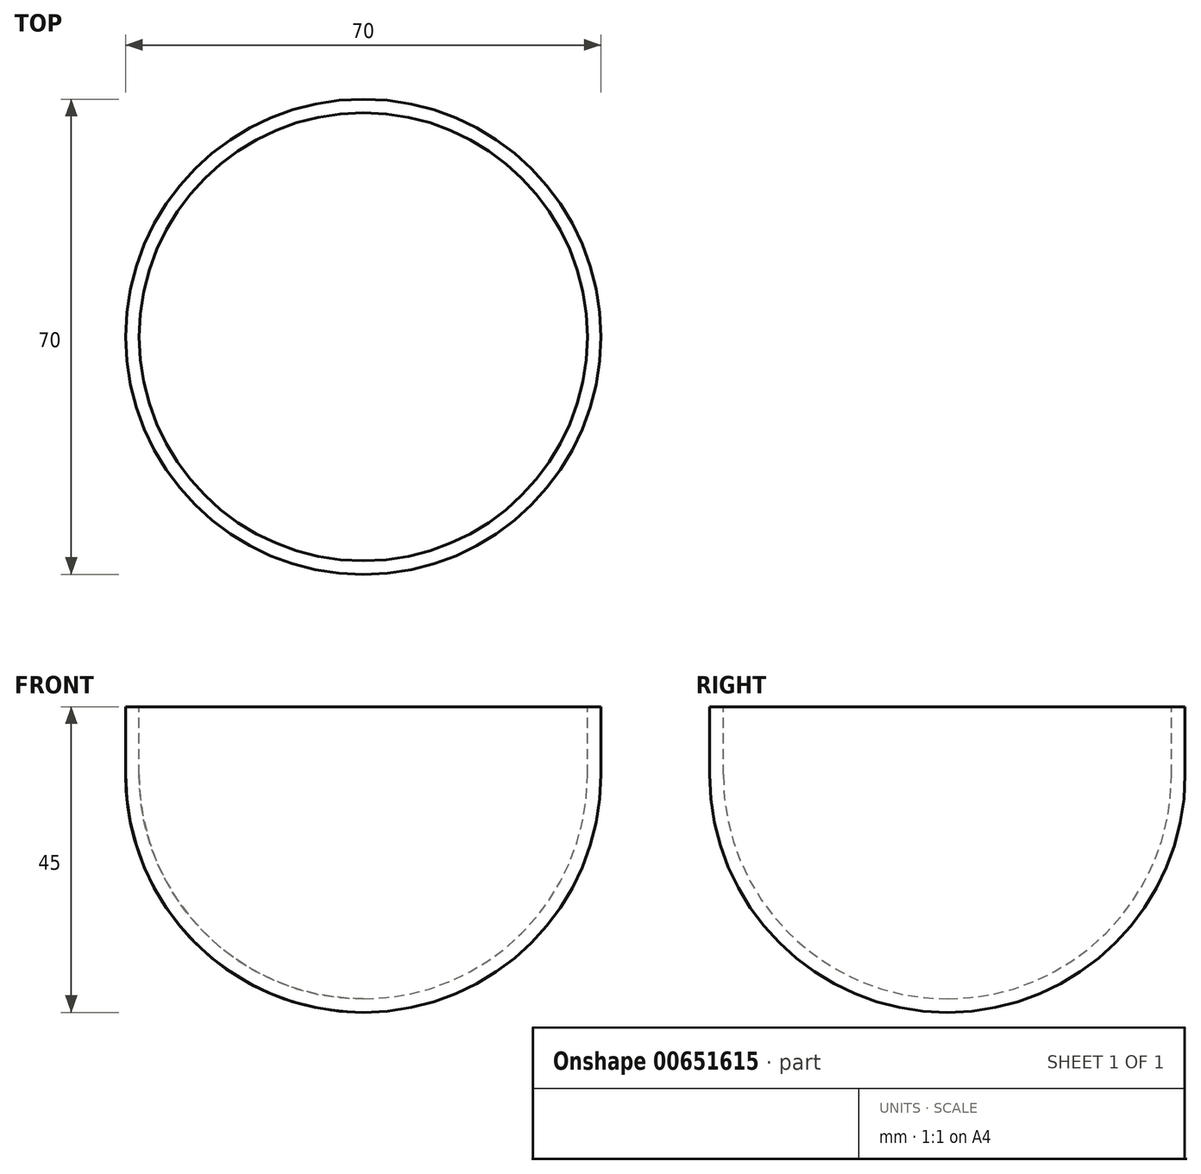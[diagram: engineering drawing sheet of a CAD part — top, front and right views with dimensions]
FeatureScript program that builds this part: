
annotation { "Feature Type Name" : "Feature", "Feature Type Description" : "" }
export const myFeature = defineFeature(function(context is Context, id is Id, definition is map)
    precondition{}
    {
        {
            var Q0;
            Q0=qCreatedBy(makeId("Front.planeOp"),FACE);
            var sketch = newSketch(context, id + "F0", { "sketchPlane" : qUnion([Q0])});
            skArc(sketch, "E0", {"start": v(0, 10) * mm, "mid": v(24.75, 20.25) * mm, "end": v(35, 45) * mm});
            skArc(sketch, "E1", {"start": v(0, 12) * mm, "mid": v(23.33, 21.67) * mm, "end": v(33, 45) * mm});
            skLineSegment(sketch, "E2", {"start": v(35, 45) * mm, "end": v(35, 55) * mm});
            skLineSegment(sketch, "E3", {"start": v(33, 45) * mm, "end": v(33, 55) * mm});
            skLineSegment(sketch, "E4", {"start": v(33, 55) * mm, "end": v(35, 55) * mm});
            skLineSegment(sketch, "E5", {"start": v(0, 12) * mm, "end": v(0, 10) * mm});
            skSolve(sketch);
        }
        {
            var Q0;
            Q0=makeQuery(id+"F0.imprint","IMPRINT",FACE,{"disambiguationData":[TD([[makeQuery(id+"F0.imprint","IMPRINT",EDGE,{"derivedFrom":sQuery(id+"F0.wireOp",EDGE,"E0")}),1.0]])]});
            var Q1;
            Q1=sQuery(id+"F0.wireOp",EDGE,"E5");
            revolve(context, id + "F1", {"entities" : qUnion([Q0]), "axis" : qUnion([Q1]), "revolveType" : RevolveType.FULL});
        }
    });
